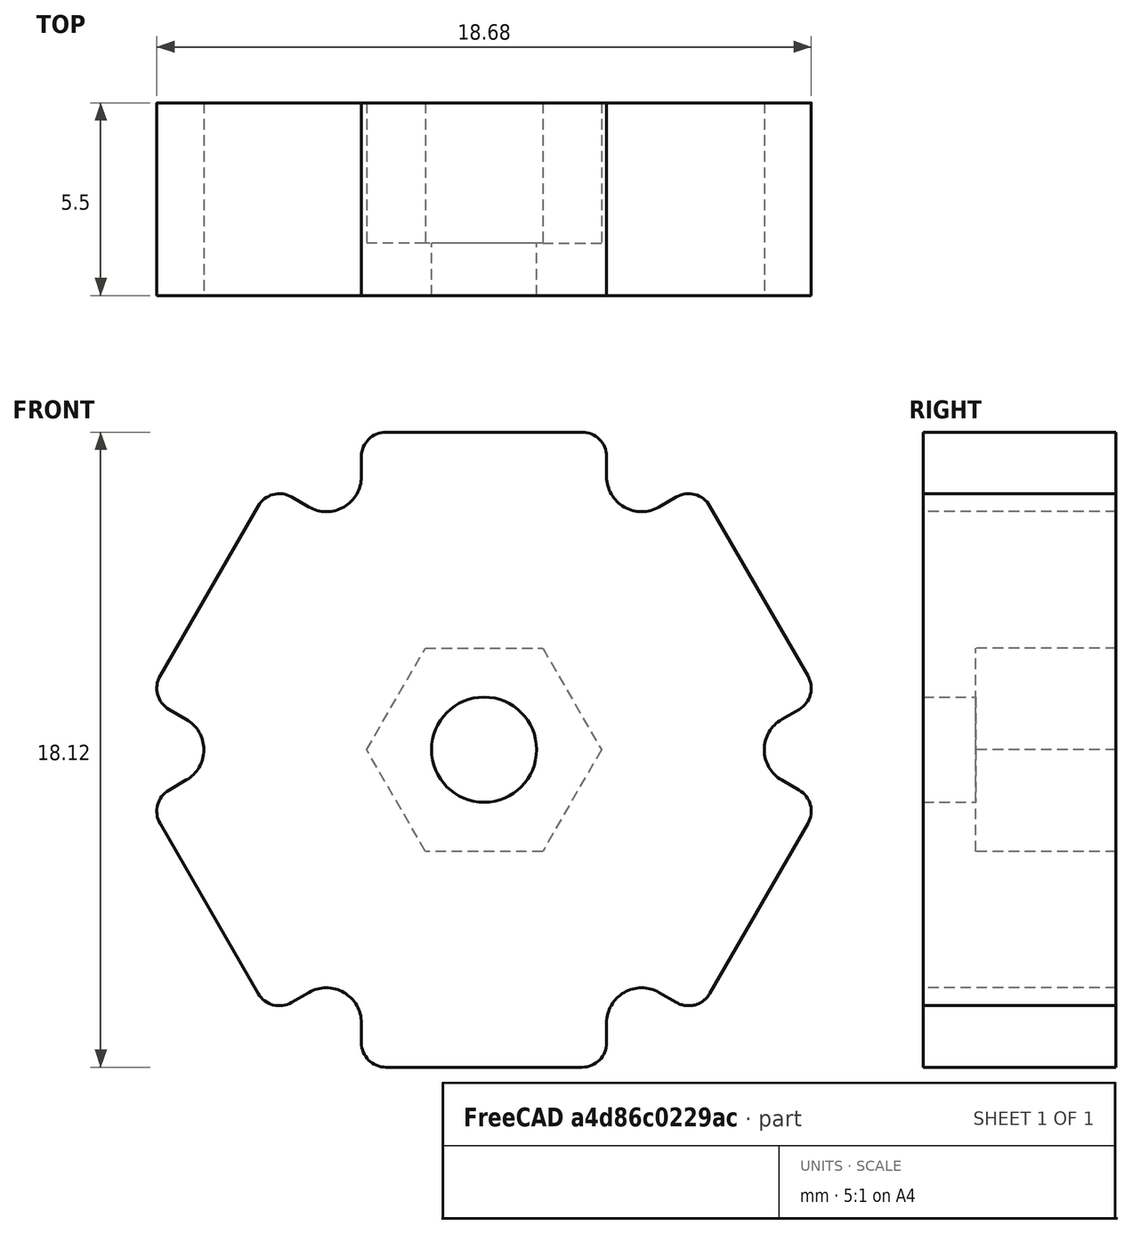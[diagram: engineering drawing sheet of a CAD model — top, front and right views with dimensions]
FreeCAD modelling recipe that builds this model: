
FCSTD DOCUMENT  (FreeCAD 0.21R33771 (Git))
Label: Thumb_tensioner
License: All rights reserved
LicenseURL: http://en.wikipedia.org/wiki/All_rights_reserved
objects: Part::Feature×1, PartDesign::FeatureBase×1, Sketcher::SketchObject×1, PartDesign::Body×1
note: 4 computed .brp shape members not serialized (recipe doc carries the construction recipe); baked Part::Feature solids carry a one-line shape summary decoded from their .brp

FEATURE [Part::Feature] Solid  label="thumb_tensioner_001"
  shape: bbox 18.68 x 5.5 x 18.12 mm, 46 faces (baked)
FEATURE [PartDesign::FeatureBase] BaseFeature
  BaseFeature = -> Solid
FEATURE [Sketcher::SketchObject] Sketch
  FullyConstrained = false
  MapMode = 5
  Placement = pos=(0,2.75015,-6e-16) rot=(0,0.707107,0.707107;3.14159rad)
  Support = -> [BaseFeature]
  sketch-geometry (8):
    g0: LineSegment StartX=-0.442339 StartY=6.26268 StartZ=0 EndX=1.45544 EndY=6.26268 EndZ=0
    g1: LineSegment StartX=1.45544 StartY=6.26268 StartZ=0 EndX=1.45544 EndY=4.66456 EndZ=0
    g2: LineSegment StartX=1.45544 StartY=4.66456 StartZ=0 EndX=-0.442339 EndY=4.66456 EndZ=0
    g3: LineSegment StartX=-0.442339 StartY=4.66456 StartZ=0 EndX=-0.442339 EndY=6.26268 EndZ=0
    g4: LineSegment StartX=-5.93591 StartY=4.63126 StartZ=0 EndX=-4.93708 EndY=4.63126 EndZ=0
    g5: LineSegment StartX=-4.93708 StartY=4.63126 StartZ=0 EndX=-4.93708 EndY=3.2329 EndZ=0
    g6: LineSegment StartX=-4.93708 StartY=3.2329 StartZ=0 EndX=-5.93591 EndY=3.2329 EndZ=0
    g7: LineSegment StartX=-5.93591 StartY=3.2329 StartZ=0 EndX=-5.93591 EndY=4.63126 EndZ=0
  constraints (16):
    c: Coincident(g0,g1)
    c: Coincident(g1,g2)
    c: Coincident(g2,g3)
    c: Coincident(g3,g0)
    c: Horizontal(g0)
    c: Horizontal(g2)
    c: Vertical(g1)
    c: Vertical(g3)
    c: Coincident(g4,g5)
    c: Coincident(g5,g6)
    c: Coincident(g6,g7)
    c: Coincident(g7,g4)
    c: Horizontal(g4)
    c: Horizontal(g6)
    c: Vertical(g5)
    c: Vertical(g7)
FEATURE [PartDesign::Body] Body
  BaseFeature = -> Solid
  Group = -> [BaseFeature,Sketch]
  Origin = -> Origin
  Tip = -> BaseFeature
